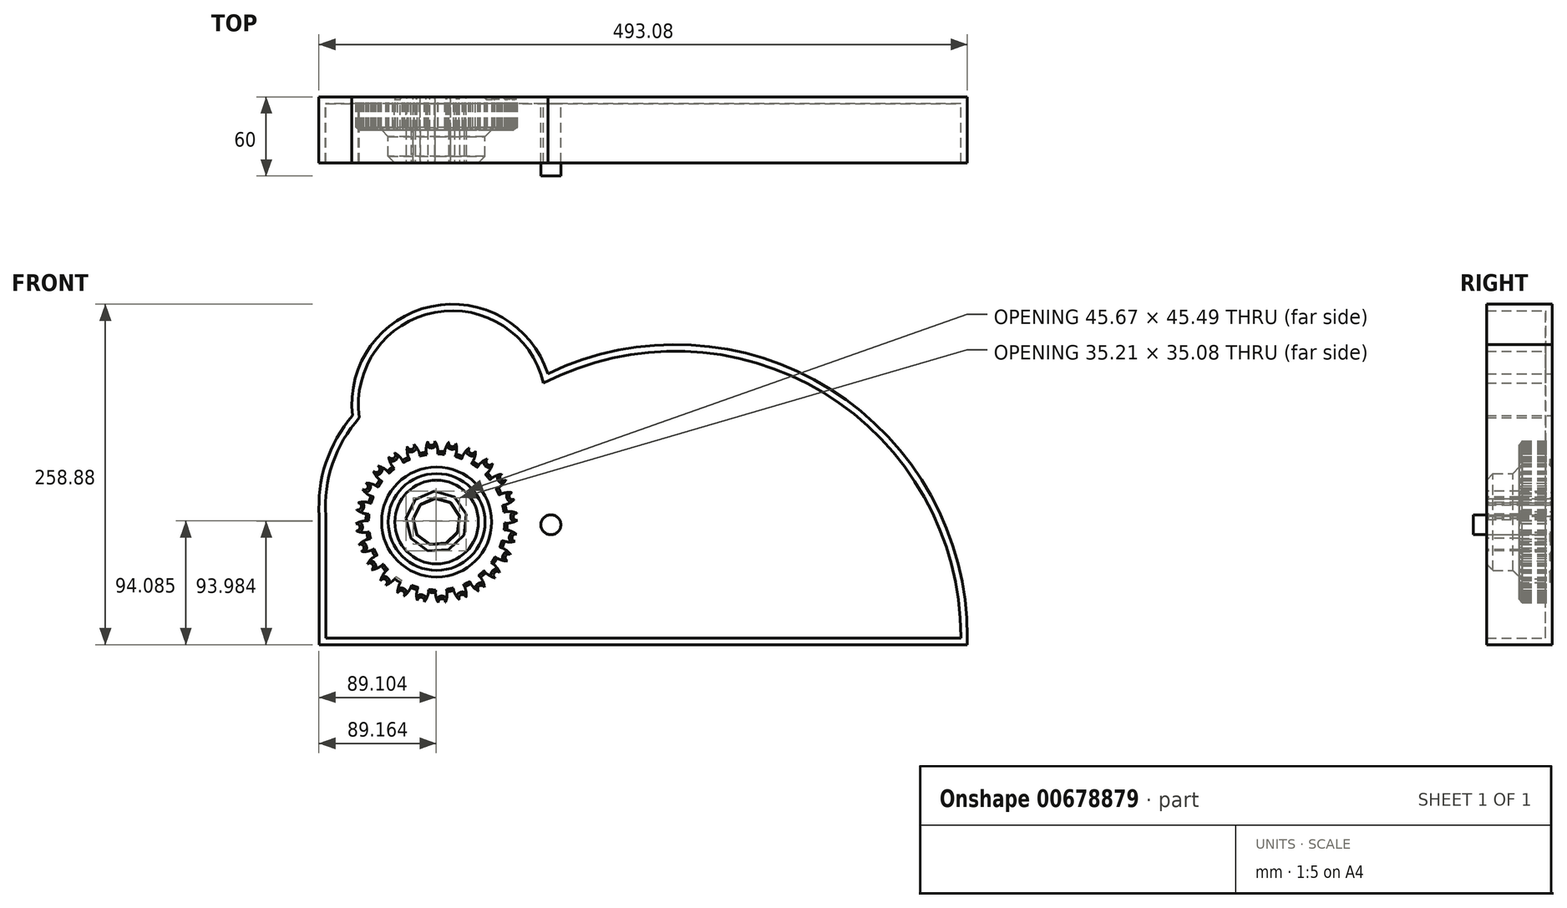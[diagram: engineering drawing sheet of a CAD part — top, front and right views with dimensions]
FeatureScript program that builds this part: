
annotation { "Feature Type Name" : "Feature", "Feature Type Description" : "" }
export const myFeature = defineFeature(function(context is Context, id is Id, definition is map)
    precondition{}
    {
        {
            var Q0;
            Q0=qCreatedBy(makeId("Front.planeOp"),FACE);
            var sketch = newSketch(context, id + "F0", { "sketchPlane" : qUnion([Q0])});
            skCircle(sketch, "E0", {"center": v(0, 0) * mm, "radius": 53.72 * mm});
            skCircle(sketch, "E1", {"center": v(0, 0) * mm, "radius": 58.67 * mm, "construction": true});
            skCircle(sketch, "E2", {"center": v(0, 0) * mm, "radius": 63.5 * mm, "construction": true});
            skLineSegment(sketch, "E3", {"start": v(0, 0) * mm, "end": v(0, 101.64) * mm, "construction": true});
            skLineSegment(sketch, "E4", {"start": v(0, 0) * mm, "end": v(-7.05, 107.5) * mm, "construction": true});
            skLineSegment(sketch, "E5", {"start": v(0, 58.67) * mm, "end": v(-85.15, 58.67) * mm, "construction": true});
            skLineSegment(sketch, "E6", {"start": v(0, 58.67) * mm, "end": v(-80.84, 29.25) * mm, "construction": true});
            skCircle(sketch, "E7", {"center": v(0, 0) * mm, "radius": 55.14 * mm, "construction": true});
            skCircle(sketch, "E8", {"center": v(0, 58.67) * mm, "radius": 14.6 * mm, "construction": true});
            skCircle(sketch, "E9", {"center": v(-13.72, 53.68) * mm, "radius": 14.6 * mm, "construction": true});
            skArc(sketch, "E10", {"start": v(0, 58.67) * mm, "mid": v(-1.19, 61.2) * mm, "end": v(-2.86, 63.44) * mm});
            skArc(sketch, "E11", {"start": v(0.88, 53.71) * mm, "mid": v(0.65, 56.23) * mm, "end": v(0, 58.67) * mm});
            skArc(sketch, "E12.MirrorCS", {"start": v(-7.66, 58.17) * mm, "mid": v(-6.8, 60.83) * mm, "end": v(-5.45, 63.27) * mm});
            skArc(sketch, "E13.MirrorCS", {"start": v(-7.88, 53.14) * mm, "mid": v(-7.98, 55.66) * mm, "end": v(-7.66, 58.17) * mm});
            skArc(sketch, "E14", {"start": v(-5.45, 63.27) * mm, "mid": v(-3.82, 58.31) * mm, "end": v(-2.86, 63.44) * mm});
            skCircle(sketch, "E15", {"center": v(0, 0) * mm, "radius": 36.8 * mm});
            skCircle(sketch, "E16.cCircle", {"center": v(0, 0) * mm, "radius": 17.92 * mm, "construction": true});
            skLineSegment(sketch, "E16.0", {"start": v(7.22, -16.4) * mm, "end": v(-5.01, -17.2) * mm});
            skLineSegment(sketch, "E16.1", {"start": v(-5.01, -17.2) * mm, "end": v(-14.9, -9.95) * mm});
            skLineSegment(sketch, "E16.2", {"start": v(-14.9, -9.95) * mm, "end": v(-17.8, 1.95) * mm});
            skLineSegment(sketch, "E16.3", {"start": v(-17.8, 1.95) * mm, "end": v(-12.39, 12.94) * mm});
            skLineSegment(sketch, "E16.4", {"start": v(-12.39, 12.94) * mm, "end": v(-1.17, 17.88) * mm});
            skLineSegment(sketch, "E16.5", {"start": v(-1.17, 17.88) * mm, "end": v(10.6, 14.45) * mm});
            skLineSegment(sketch, "E16.6", {"start": v(10.6, 14.45) * mm, "end": v(17.4, 4.26) * mm});
            skLineSegment(sketch, "E16.7", {"start": v(17.4, 4.26) * mm, "end": v(16.07, -7.92) * mm});
            skLineSegment(sketch, "E16.8", {"start": v(16.07, -7.92) * mm, "end": v(7.22, -16.4) * mm});
            skSolve(sketch);
        }
        {
            var Q0;
            {var subQ0=sQuery(id+"F0.wireOp",EDGE,"E0");var subQ1=makeQuery(id+"F0.imprint","INTERSECT",VERTEX,{"derivedFrom":[subQ0,sQuery(id+"F0.wireOp",EDGE,"E11")]});Q0=makeQuery(id+"F0.imprint","IMPRINT",FACE,{"disambiguationData":[TD([[makeQuery(id+"F0.imprint","IMPRINT",EDGE,{"disambiguationData":[TD([[subQ1,-1.0]])],"derivedFrom":subQ0}),1.0]])]});}
            var Q1;
            Q1=makeQuery(id+"F0.imprint","IMPRINT",FACE,{"disambiguationData":[TD([[makeQuery(id+"F0.imprint","IMPRINT",EDGE,{"derivedFrom":sQuery(id+"F0.wireOp",EDGE,"E10")}),1.0]])]});
            extrude(context, id + "F1", {"entities" : qUnion([Q0, Q1]), "depth" : 25 * mm, "offsetDistance" : 25 * mm});
        }
        {
            var Q0;
            Q0=makeQuery(id+"F1.opExtrude","SWEPT_BODY",BODY,{"disambiguationData":[OSD([sQuery(id+"F0.wireOp",EDGE,"E0"),sQuery(id+"F0.wireOp",EDGE,"E10"),sQuery(id+"F0.wireOp",EDGE,"E11"),sQuery(id+"F0.wireOp",EDGE,"E12.MirrorCS"),sQuery(id+"F0.wireOp",EDGE,"E13.MirrorCS"),sQuery(id+"F0.wireOp",EDGE,"E14")])]});
            var Q1;
            Q1=makeQuery(id+"F1.opExtrude","SWEPT_FACE",FACE,{"disambiguationData":[OSD([sQuery(id+"F0.wireOp",EDGE,"E0")])]});
            circularPattern(context, id + "F2", {"entities" : qUnion([Q0]), "axis" : qUnion([Q1]), "angle" : 360 * degree, "instanceCount" : 24, "equalSpace" : true});
        }
        {
            var Q0;
            Q0=makeQuery(id+"F0.imprint","IMPRINT",FACE,{"disambiguationData":[TD([[makeQuery(id+"F0.imprint","IMPRINT",EDGE,{"derivedFrom":sQuery(id+"F0.wireOp",EDGE,"E15")}),1.0]])]});
            extrude(context, id + "F3", {"entities" : qUnion([Q0]), "operationType" : NewBodyOperationType.ADD, "depth" : 50 * mm, "offsetDistance" : 25 * mm});
        }
        {
            var Q0;
            Q0=makeQuery(id+"F3.opExtrude","CAP_EDGE",EDGE,{"disambiguationData":[OSD([sQuery(id+"F0.wireOp",EDGE,"E15")])],"isStart":false});
            var Q1;
            Q1=makeQuery(id+"F3.opExtrude","SWEPT_FACE",FACE,{"disambiguationData":[OSD([sQuery(id+"F0.wireOp",EDGE,"E15")])]});
            chamfer(context, id + "F4", {"entities" : qUnion([Q0, Q1]), "width" : 5 * mm, "tangentPropagation" : true});
        }
        {
            var Q0;
            Q0=makeQuery(id+"F2.opPattern","COPY",EDGE,{"derivedFrom":makeQuery(id+"F1.opExtrude","CAP_EDGE",EDGE,{"disambiguationData":[OSD([sQuery(id+"F0.wireOp",EDGE,"E14")])],"isStart":false}),"instanceName":"20"});
            var Q1;
            Q1=makeQuery(id+"F2.opPattern","COPY",EDGE,{"derivedFrom":makeQuery(id+"F1.opExtrude","CAP_EDGE",EDGE,{"disambiguationData":[OSD([sQuery(id+"F0.wireOp",EDGE,"E14")])],"isStart":false}),"instanceName":"10"});
            var Q2;
            Q2=makeQuery(id+"F2.opPattern","COPY",EDGE,{"derivedFrom":makeQuery(id+"F1.opExtrude","CAP_EDGE",EDGE,{"disambiguationData":[OSD([sQuery(id+"F0.wireOp",EDGE,"E14")])],"isStart":true}),"instanceName":"9"});
            var Q3;
            Q3=makeQuery(id+"F2.opPattern","COPY",EDGE,{"derivedFrom":makeQuery(id+"F1.opExtrude","CAP_EDGE",EDGE,{"disambiguationData":[OSD([sQuery(id+"F0.wireOp",EDGE,"E14")])],"isStart":true}),"instanceName":"8"});
            var Q4;
            Q4=makeQuery(id+"F2.opPattern","COPY",EDGE,{"derivedFrom":makeQuery(id+"F1.opExtrude","CAP_EDGE",EDGE,{"disambiguationData":[OSD([sQuery(id+"F0.wireOp",EDGE,"E14")])],"isStart":true}),"instanceName":"7"});
            var Q5;
            Q5=makeQuery(id+"F2.opPattern","COPY",EDGE,{"derivedFrom":makeQuery(id+"F1.opExtrude","CAP_EDGE",EDGE,{"disambiguationData":[OSD([sQuery(id+"F0.wireOp",EDGE,"E14")])],"isStart":false}),"instanceName":"14"});
            var Q6;
            Q6=makeQuery(id+"F2.opPattern","COPY",EDGE,{"derivedFrom":makeQuery(id+"F1.opExtrude","CAP_EDGE",EDGE,{"disambiguationData":[OSD([sQuery(id+"F0.wireOp",EDGE,"E14")])],"isStart":false}),"instanceName":"11"});
            var Q7;
            Q7=makeQuery(id+"F2.opPattern","COPY",EDGE,{"derivedFrom":makeQuery(id+"F1.opExtrude","CAP_EDGE",EDGE,{"disambiguationData":[OSD([sQuery(id+"F0.wireOp",EDGE,"E14")])],"isStart":false}),"instanceName":"9"});
            var Q8;
            Q8=makeQuery(id+"F2.opPattern","COPY",EDGE,{"derivedFrom":makeQuery(id+"F1.opExtrude","CAP_EDGE",EDGE,{"disambiguationData":[OSD([sQuery(id+"F0.wireOp",EDGE,"E14")])],"isStart":false}),"instanceName":"8"});
            var Q9;
            Q9=makeQuery(id+"F2.opPattern","COPY",EDGE,{"derivedFrom":makeQuery(id+"F1.opExtrude","CAP_EDGE",EDGE,{"disambiguationData":[OSD([sQuery(id+"F0.wireOp",EDGE,"E14")])],"isStart":false}),"instanceName":"7"});
            var Q10;
            {var subQ1=sQuery(id+"F0.wireOp",EDGE,"E11");var subQ2=sQuery(id+"F0.wireOp",EDGE,"E0");Q10=makeQuery(id+"F3.boolean.opBoolean","SPLIT",EDGE,{"disambiguationData":[TD([makeQuery(id+"F2.opPattern","COPY",FACE,{"derivedFrom":makeQuery(id+"F1.opExtrude","SWEPT_FACE",FACE,{"disambiguationData":[OSD([subQ1])]}),"instanceName":"13"})])],"derivedFrom":makeQuery(id+"F1.opExtrude","CAP_EDGE",EDGE,{"disambiguationData":[OSD([subQ2])],"isStart":false})});}
            var Q11;
            {var subQ2=sQuery(id+"F0.wireOp",EDGE,"E11");var subQ3=sQuery(id+"F0.wireOp",EDGE,"E0");Q11=makeQuery(id+"F3.boolean.opBoolean","SPLIT",EDGE,{"disambiguationData":[TD([makeQuery(id+"F2.opPattern","COPY",FACE,{"derivedFrom":makeQuery(id+"F1.opExtrude","SWEPT_FACE",FACE,{"disambiguationData":[OSD([subQ2])]}),"instanceName":"14"})])],"derivedFrom":makeQuery(id+"F1.opExtrude","CAP_EDGE",EDGE,{"disambiguationData":[OSD([subQ3])],"isStart":true})});}
            var Q12;
            {var subQ1=sQuery(id+"F0.wireOp",EDGE,"E11");var subQ2=sQuery(id+"F0.wireOp",EDGE,"E0");Q12=makeQuery(id+"F3.boolean.opBoolean","SPLIT",EDGE,{"disambiguationData":[TD([makeQuery(id+"F2.opPattern","COPY",FACE,{"derivedFrom":makeQuery(id+"F1.opExtrude","SWEPT_FACE",FACE,{"disambiguationData":[OSD([subQ1])]}),"instanceName":"15"})])],"derivedFrom":makeQuery(id+"F1.opExtrude","CAP_EDGE",EDGE,{"disambiguationData":[OSD([subQ2])],"isStart":false})});}
            var Q13;
            {var subQ1=sQuery(id+"F0.wireOp",EDGE,"E11");var subQ2=sQuery(id+"F0.wireOp",EDGE,"E0");Q13=makeQuery(id+"F3.boolean.opBoolean","SPLIT",EDGE,{"disambiguationData":[TD([makeQuery(id+"F2.opPattern","COPY",FACE,{"derivedFrom":makeQuery(id+"F1.opExtrude","SWEPT_FACE",FACE,{"disambiguationData":[OSD([subQ1])]}),"instanceName":"18"})])],"derivedFrom":makeQuery(id+"F1.opExtrude","CAP_EDGE",EDGE,{"disambiguationData":[OSD([subQ2])],"isStart":false})});}
            var Q14;
            {var subQ1=sQuery(id+"F0.wireOp",EDGE,"E11");var subQ2=sQuery(id+"F0.wireOp",EDGE,"E0");Q14=makeQuery(id+"F3.boolean.opBoolean","SPLIT",EDGE,{"disambiguationData":[TD([makeQuery(id+"F2.opPattern","COPY",FACE,{"derivedFrom":makeQuery(id+"F1.opExtrude","SWEPT_FACE",FACE,{"disambiguationData":[OSD([subQ1])]}),"instanceName":"19"})])],"derivedFrom":makeQuery(id+"F1.opExtrude","CAP_EDGE",EDGE,{"disambiguationData":[OSD([subQ2])],"isStart":false})});}
            var Q15;
            {var subQ1=sQuery(id+"F0.wireOp",EDGE,"E11");var subQ2=sQuery(id+"F0.wireOp",EDGE,"E0");Q15=makeQuery(id+"F3.boolean.opBoolean","SPLIT",EDGE,{"disambiguationData":[TD([makeQuery(id+"F2.opPattern","COPY",FACE,{"derivedFrom":makeQuery(id+"F1.opExtrude","SWEPT_FACE",FACE,{"disambiguationData":[OSD([subQ1])]}),"instanceName":"20"})])],"derivedFrom":makeQuery(id+"F1.opExtrude","CAP_EDGE",EDGE,{"disambiguationData":[OSD([subQ2])],"isStart":false})});}
            var Q16;
            Q16=makeQuery(id+"F2.opPattern","COPY",EDGE,{"derivedFrom":makeQuery(id+"F1.opExtrude","CAP_EDGE",EDGE,{"disambiguationData":[OSD([sQuery(id+"F0.wireOp",EDGE,"E14")])],"isStart":false}),"instanceName":"22"});
            var Q17;
            Q17=makeQuery(id+"F2.opPattern","COPY",EDGE,{"derivedFrom":makeQuery(id+"F1.opExtrude","CAP_EDGE",EDGE,{"disambiguationData":[OSD([sQuery(id+"F0.wireOp",EDGE,"E14")])],"isStart":false}),"instanceName":"23"});
            var Q18;
            Q18=makeQuery(id+"F1.opExtrude","CAP_EDGE",EDGE,{"disambiguationData":[OSD([sQuery(id+"F0.wireOp",EDGE,"E14")])],"isStart":false});
            var Q19;
            Q19=makeQuery(id+"F2.opPattern","COPY",EDGE,{"derivedFrom":makeQuery(id+"F1.opExtrude","CAP_EDGE",EDGE,{"disambiguationData":[OSD([sQuery(id+"F0.wireOp",EDGE,"E14")])],"isStart":false}),"instanceName":"13"});
            var Q20;
            Q20=makeQuery(id+"F2.opPattern","COPY",EDGE,{"derivedFrom":makeQuery(id+"F1.opExtrude","CAP_EDGE",EDGE,{"disambiguationData":[OSD([sQuery(id+"F0.wireOp",EDGE,"E14")])],"isStart":false}),"instanceName":"12"});
            var Q21;
            {var subQ1=sQuery(id+"F0.wireOp",EDGE,"E11");var subQ2=sQuery(id+"F0.wireOp",EDGE,"E0");Q21=makeQuery(id+"F3.boolean.opBoolean","SPLIT",EDGE,{"disambiguationData":[TD([makeQuery(id+"F2.opPattern","COPY",FACE,{"derivedFrom":makeQuery(id+"F1.opExtrude","SWEPT_FACE",FACE,{"disambiguationData":[OSD([subQ1])]}),"instanceName":"12"})])],"derivedFrom":makeQuery(id+"F1.opExtrude","CAP_EDGE",EDGE,{"disambiguationData":[OSD([subQ2])],"isStart":false})});}
            var Q22;
            {var subQ1=sQuery(id+"F0.wireOp",EDGE,"E11");var subQ2=sQuery(id+"F0.wireOp",EDGE,"E0");Q22=makeQuery(id+"F3.boolean.opBoolean","SPLIT",EDGE,{"disambiguationData":[TD([makeQuery(id+"F2.opPattern","COPY",FACE,{"derivedFrom":makeQuery(id+"F1.opExtrude","SWEPT_FACE",FACE,{"disambiguationData":[OSD([subQ1])]}),"instanceName":"11"})])],"derivedFrom":makeQuery(id+"F1.opExtrude","CAP_EDGE",EDGE,{"disambiguationData":[OSD([subQ2])],"isStart":false})});}
            var Q23;
            {var subQ1=sQuery(id+"F0.wireOp",EDGE,"E11");var subQ2=sQuery(id+"F0.wireOp",EDGE,"E0");Q23=makeQuery(id+"F3.boolean.opBoolean","SPLIT",EDGE,{"disambiguationData":[TD([makeQuery(id+"F2.opPattern","COPY",FACE,{"derivedFrom":makeQuery(id+"F1.opExtrude","SWEPT_FACE",FACE,{"disambiguationData":[OSD([subQ1])]}),"instanceName":"10"})])],"derivedFrom":makeQuery(id+"F1.opExtrude","CAP_EDGE",EDGE,{"disambiguationData":[OSD([subQ2])],"isStart":false})});}
            var Q24;
            {var subQ1=sQuery(id+"F0.wireOp",EDGE,"E11");var subQ2=sQuery(id+"F0.wireOp",EDGE,"E0");Q24=makeQuery(id+"F3.boolean.opBoolean","SPLIT",EDGE,{"disambiguationData":[TD([makeQuery(id+"F2.opPattern","COPY",FACE,{"derivedFrom":makeQuery(id+"F1.opExtrude","SWEPT_FACE",FACE,{"disambiguationData":[OSD([subQ1])]}),"instanceName":"9"})])],"derivedFrom":makeQuery(id+"F1.opExtrude","CAP_EDGE",EDGE,{"disambiguationData":[OSD([subQ2])],"isStart":false})});}
            var Q25;
            {var subQ1=sQuery(id+"F0.wireOp",EDGE,"E11");var subQ2=sQuery(id+"F0.wireOp",EDGE,"E0");Q25=makeQuery(id+"F3.boolean.opBoolean","SPLIT",EDGE,{"disambiguationData":[TD([makeQuery(id+"F2.opPattern","COPY",FACE,{"derivedFrom":makeQuery(id+"F1.opExtrude","SWEPT_FACE",FACE,{"disambiguationData":[OSD([subQ1])]}),"instanceName":"8"})])],"derivedFrom":makeQuery(id+"F1.opExtrude","CAP_EDGE",EDGE,{"disambiguationData":[OSD([subQ2])],"isStart":false})});}
            var Q26;
            {var subQ1=sQuery(id+"F0.wireOp",EDGE,"E11");var subQ2=sQuery(id+"F0.wireOp",EDGE,"E0");Q26=makeQuery(id+"F3.boolean.opBoolean","SPLIT",EDGE,{"disambiguationData":[TD([makeQuery(id+"F2.opPattern","COPY",FACE,{"derivedFrom":makeQuery(id+"F1.opExtrude","SWEPT_FACE",FACE,{"disambiguationData":[OSD([subQ1])]}),"instanceName":"7"})])],"derivedFrom":makeQuery(id+"F1.opExtrude","CAP_EDGE",EDGE,{"disambiguationData":[OSD([subQ2])],"isStart":false})});}
            var Q27;
            {var subQ1=sQuery(id+"F0.wireOp",EDGE,"E11");var subQ2=sQuery(id+"F0.wireOp",EDGE,"E0");Q27=makeQuery(id+"F3.boolean.opBoolean","SPLIT",EDGE,{"disambiguationData":[TD([makeQuery(id+"F2.opPattern","COPY",FACE,{"derivedFrom":makeQuery(id+"F1.opExtrude","SWEPT_FACE",FACE,{"disambiguationData":[OSD([subQ1])]}),"instanceName":"6"})])],"derivedFrom":makeQuery(id+"F1.opExtrude","CAP_EDGE",EDGE,{"disambiguationData":[OSD([subQ2])],"isStart":false})});}
            var Q28;
            Q28=makeQuery(id+"F2.opPattern","COPY",EDGE,{"derivedFrom":makeQuery(id+"F1.opExtrude","CAP_EDGE",EDGE,{"disambiguationData":[OSD([sQuery(id+"F0.wireOp",EDGE,"E14")])],"isStart":false}),"instanceName":"6"});
            var Q29;
            Q29=makeQuery(id+"F2.opPattern","COPY",EDGE,{"derivedFrom":makeQuery(id+"F1.opExtrude","CAP_EDGE",EDGE,{"disambiguationData":[OSD([sQuery(id+"F0.wireOp",EDGE,"E14")])],"isStart":false}),"instanceName":"5"});
            var Q30;
            {var subQ1=sQuery(id+"F0.wireOp",EDGE,"E11");var subQ2=sQuery(id+"F0.wireOp",EDGE,"E0");Q30=makeQuery(id+"F3.boolean.opBoolean","SPLIT",EDGE,{"disambiguationData":[TD([makeQuery(id+"F2.opPattern","COPY",FACE,{"derivedFrom":makeQuery(id+"F1.opExtrude","SWEPT_FACE",FACE,{"disambiguationData":[OSD([subQ1])]}),"instanceName":"4"})])],"derivedFrom":makeQuery(id+"F1.opExtrude","CAP_EDGE",EDGE,{"disambiguationData":[OSD([subQ2])],"isStart":false})});}
            var Q31;
            {var subQ1=sQuery(id+"F0.wireOp",EDGE,"E11");var subQ2=sQuery(id+"F0.wireOp",EDGE,"E0");Q31=makeQuery(id+"F3.boolean.opBoolean","SPLIT",EDGE,{"disambiguationData":[TD([makeQuery(id+"F2.opPattern","COPY",FACE,{"derivedFrom":makeQuery(id+"F1.opExtrude","SWEPT_FACE",FACE,{"disambiguationData":[OSD([subQ1])]}),"instanceName":"5"})])],"derivedFrom":makeQuery(id+"F1.opExtrude","CAP_EDGE",EDGE,{"disambiguationData":[OSD([subQ2])],"isStart":false})});}
            var Q32;
            Q32=makeQuery(id+"F2.opPattern","COPY",EDGE,{"derivedFrom":makeQuery(id+"F1.opExtrude","CAP_EDGE",EDGE,{"disambiguationData":[OSD([sQuery(id+"F0.wireOp",EDGE,"E14")])],"isStart":false}),"instanceName":"21"});
            var Q33;
            {var subQ1=sQuery(id+"F0.wireOp",EDGE,"E11");var subQ2=sQuery(id+"F0.wireOp",EDGE,"E0");Q33=makeQuery(id+"F3.boolean.opBoolean","SPLIT",EDGE,{"disambiguationData":[TD([makeQuery(id+"F2.opPattern","COPY",FACE,{"derivedFrom":makeQuery(id+"F1.opExtrude","SWEPT_FACE",FACE,{"disambiguationData":[OSD([subQ1])]}),"instanceName":"21"})])],"derivedFrom":makeQuery(id+"F1.opExtrude","CAP_EDGE",EDGE,{"disambiguationData":[OSD([subQ2])],"isStart":false})});}
            var Q34;
            {var subQ1=sQuery(id+"F0.wireOp",EDGE,"E11");var subQ2=sQuery(id+"F0.wireOp",EDGE,"E0");Q34=makeQuery(id+"F3.boolean.opBoolean","SPLIT",EDGE,{"disambiguationData":[TD([makeQuery(id+"F2.opPattern","COPY",FACE,{"derivedFrom":makeQuery(id+"F1.opExtrude","SWEPT_FACE",FACE,{"disambiguationData":[OSD([subQ1])]}),"instanceName":"22"})])],"derivedFrom":makeQuery(id+"F1.opExtrude","CAP_EDGE",EDGE,{"disambiguationData":[OSD([subQ2])],"isStart":false})});}
            var Q35;
            Q35=makeQuery(id+"F2.opPattern","COPY",EDGE,{"derivedFrom":makeQuery(id+"F1.opExtrude","CAP_EDGE",EDGE,{"disambiguationData":[OSD([sQuery(id+"F0.wireOp",EDGE,"E14")])],"isStart":false}),"instanceName":"18"});
            var Q36;
            Q36=makeQuery(id+"F2.opPattern","COPY",EDGE,{"derivedFrom":makeQuery(id+"F1.opExtrude","CAP_EDGE",EDGE,{"disambiguationData":[OSD([sQuery(id+"F0.wireOp",EDGE,"E14")])],"isStart":false}),"instanceName":"17"});
            var Q37;
            Q37=makeQuery(id+"F2.opPattern","COPY",EDGE,{"derivedFrom":makeQuery(id+"F1.opExtrude","CAP_EDGE",EDGE,{"disambiguationData":[OSD([sQuery(id+"F0.wireOp",EDGE,"E14")])],"isStart":false}),"instanceName":"16"});
            var Q38;
            {var subQ1=sQuery(id+"F0.wireOp",EDGE,"E11");var subQ2=sQuery(id+"F0.wireOp",EDGE,"E0");Q38=makeQuery(id+"F3.boolean.opBoolean","SPLIT",EDGE,{"disambiguationData":[TD([makeQuery(id+"F2.opPattern","COPY",FACE,{"derivedFrom":makeQuery(id+"F1.opExtrude","SWEPT_FACE",FACE,{"disambiguationData":[OSD([subQ1])]}),"instanceName":"16"})])],"derivedFrom":makeQuery(id+"F1.opExtrude","CAP_EDGE",EDGE,{"disambiguationData":[OSD([subQ2])],"isStart":false})});}
            var Q39;
            {var subQ1=sQuery(id+"F0.wireOp",EDGE,"E11");var subQ2=sQuery(id+"F0.wireOp",EDGE,"E0");Q39=makeQuery(id+"F3.boolean.opBoolean","SPLIT",EDGE,{"disambiguationData":[TD([makeQuery(id+"F2.opPattern","COPY",FACE,{"derivedFrom":makeQuery(id+"F1.opExtrude","SWEPT_FACE",FACE,{"disambiguationData":[OSD([subQ1])]}),"instanceName":"17"})])],"derivedFrom":makeQuery(id+"F1.opExtrude","CAP_EDGE",EDGE,{"disambiguationData":[OSD([subQ2])],"isStart":false})});}
            var Q40;
            {var subQ0=sQuery(id+"F0.wireOp",EDGE,"E13.MirrorCS");var subQ2=sQuery(id+"F0.wireOp",EDGE,"E0");Q40=makeQuery(id+"F3.boolean.opBoolean","SPLIT",EDGE,{"disambiguationData":[TD([makeQuery(id+"F1.opExtrude","SWEPT_FACE",FACE,{"disambiguationData":[OSD([subQ0])]})])],"derivedFrom":makeQuery(id+"F1.opExtrude","CAP_EDGE",EDGE,{"disambiguationData":[OSD([subQ2])],"isStart":false})});}
            var Q41;
            {var subQ1=sQuery(id+"F0.wireOp",EDGE,"E11");var subQ2=sQuery(id+"F0.wireOp",EDGE,"E0");Q41=makeQuery(id+"F3.boolean.opBoolean","SPLIT",EDGE,{"disambiguationData":[TD([makeQuery(id+"F1.opExtrude","SWEPT_FACE",FACE,{"disambiguationData":[OSD([subQ1])]})])],"derivedFrom":makeQuery(id+"F1.opExtrude","CAP_EDGE",EDGE,{"disambiguationData":[OSD([subQ2])],"isStart":false})});}
            var Q42;
            {var subQ1=sQuery(id+"F0.wireOp",EDGE,"E11");var subQ2=sQuery(id+"F0.wireOp",EDGE,"E0");Q42=makeQuery(id+"F3.boolean.opBoolean","SPLIT",EDGE,{"disambiguationData":[TD([makeQuery(id+"F2.opPattern","COPY",FACE,{"derivedFrom":makeQuery(id+"F1.opExtrude","SWEPT_FACE",FACE,{"disambiguationData":[OSD([subQ1])]}),"instanceName":"1"})])],"derivedFrom":makeQuery(id+"F1.opExtrude","CAP_EDGE",EDGE,{"disambiguationData":[OSD([subQ2])],"isStart":false})});}
            var Q43;
            {var subQ1=sQuery(id+"F0.wireOp",EDGE,"E11");var subQ2=sQuery(id+"F0.wireOp",EDGE,"E0");Q43=makeQuery(id+"F3.boolean.opBoolean","SPLIT",EDGE,{"disambiguationData":[TD([makeQuery(id+"F2.opPattern","COPY",FACE,{"derivedFrom":makeQuery(id+"F1.opExtrude","SWEPT_FACE",FACE,{"disambiguationData":[OSD([subQ1])]}),"instanceName":"2"})])],"derivedFrom":makeQuery(id+"F1.opExtrude","CAP_EDGE",EDGE,{"disambiguationData":[OSD([subQ2])],"isStart":false})});}
            var Q44;
            Q44=makeQuery(id+"F2.opPattern","COPY",EDGE,{"derivedFrom":makeQuery(id+"F1.opExtrude","CAP_EDGE",EDGE,{"disambiguationData":[OSD([sQuery(id+"F0.wireOp",EDGE,"E14")])],"isStart":false}),"instanceName":"1"});
            var Q45;
            Q45=makeQuery(id+"F2.opPattern","COPY",EDGE,{"derivedFrom":makeQuery(id+"F1.opExtrude","CAP_EDGE",EDGE,{"disambiguationData":[OSD([sQuery(id+"F0.wireOp",EDGE,"E14")])],"isStart":false}),"instanceName":"2"});
            var Q46;
            Q46=makeQuery(id+"F2.opPattern","COPY",EDGE,{"derivedFrom":makeQuery(id+"F1.opExtrude","CAP_EDGE",EDGE,{"disambiguationData":[OSD([sQuery(id+"F0.wireOp",EDGE,"E14")])],"isStart":true}),"instanceName":"3"});
            var Q47;
            Q47=makeQuery(id+"F2.opPattern","COPY",EDGE,{"derivedFrom":makeQuery(id+"F1.opExtrude","CAP_EDGE",EDGE,{"disambiguationData":[OSD([sQuery(id+"F0.wireOp",EDGE,"E14")])],"isStart":false}),"instanceName":"15"});
            var Q48;
            {var subQ1=sQuery(id+"F0.wireOp",EDGE,"E11");var subQ2=sQuery(id+"F0.wireOp",EDGE,"E0");Q48=makeQuery(id+"F3.boolean.opBoolean","SPLIT",EDGE,{"disambiguationData":[TD([makeQuery(id+"F2.opPattern","COPY",FACE,{"derivedFrom":makeQuery(id+"F1.opExtrude","SWEPT_FACE",FACE,{"disambiguationData":[OSD([subQ1])]}),"instanceName":"3"})])],"derivedFrom":makeQuery(id+"F1.opExtrude","CAP_EDGE",EDGE,{"disambiguationData":[OSD([subQ2])],"isStart":false})});}
            var Q49;
            Q49=makeQuery(id+"F2.opPattern","COPY",EDGE,{"derivedFrom":makeQuery(id+"F1.opExtrude","CAP_EDGE",EDGE,{"disambiguationData":[OSD([sQuery(id+"F0.wireOp",EDGE,"E14")])],"isStart":false}),"instanceName":"4"});
            var Q50;
            Q50=makeQuery(id+"F2.opPattern","COPY",EDGE,{"derivedFrom":makeQuery(id+"F1.opExtrude","CAP_EDGE",EDGE,{"disambiguationData":[OSD([sQuery(id+"F0.wireOp",EDGE,"E14")])],"isStart":false}),"instanceName":"19"});
            var Q51;
            Q51=makeQuery(id+"F2.opPattern","COPY",EDGE,{"derivedFrom":makeQuery(id+"F1.opExtrude","CAP_EDGE",EDGE,{"disambiguationData":[OSD([sQuery(id+"F0.wireOp",EDGE,"E14")])],"isStart":false}),"instanceName":"3"});
            chamfer(context, id + "F5", {"entities" : qUnion([Q0, Q1, Q2, Q3, Q4, Q5, Q6, Q7, Q8, Q9, Q10, Q11, Q12, Q13, Q14, Q15, Q16, Q17, Q18, Q19, Q20, Q21, Q22, Q23, Q24, Q25, Q26, Q27, Q28, Q29, Q30, Q31, Q32, Q33, Q34, Q35, Q36, Q37, Q38, Q39, Q40, Q41, Q42, Q43, Q44, Q45, Q46, Q47, Q48, Q49, Q50, Q51]), "width" : 2 * mm, "tangentPropagation" : true});
        }
        {
            var Q0;
            Q0=qCreatedBy(makeId("Front.planeOp"),FACE);
            var sketch = newSketch(context, id + "F6", { "sketchPlane" : qUnion([Q0])});
            skLineSegment(sketch, "E17", {"start": v(-89.2, -93.22) * mm, "end": v(403.6, -93.22) * mm});
            skLineSegment(sketch, "E18", {"start": v(403.6, -93.22) * mm, "end": v(403.6, -87.36) * mm});
            skLineSegment(sketch, "E19", {"start": v(-89.2, -93.22) * mm, "end": v(-89.2, 4.46) * mm});
            skArc(sketch, "E20", {"start": v(-64, 80.81) * mm, "mid": v(-84.17, 45.14) * mm, "end": v(-89.2, 4.46) * mm});
            skArc(sketch, "E21", {"start": v(84.54, 112.77) * mm, "mid": v(-4.18, 163.96) * mm, "end": v(-64, 80.81) * mm});
            skArc(sketch, "E22", {"start": v(403.6, -87.36) * mm, "mid": v(299.43, 100.95) * mm, "end": v(84.54, 112.77) * mm});
            skLineSegment(sketch, "E23.0", {"start": v(7.1, -15.97) * mm, "end": v(-5.13, -16.77) * mm});
            skLineSegment(sketch, "E23.1", {"start": v(-5.13, -16.77) * mm, "end": v(-15, -9.53) * mm});
            skLineSegment(sketch, "E23.2", {"start": v(-15, -9.53) * mm, "end": v(-17.92, 2.38) * mm});
            skLineSegment(sketch, "E23.3", {"start": v(-17.92, 2.38) * mm, "end": v(-12.5, 13.37) * mm});
            skLineSegment(sketch, "E23.4", {"start": v(-12.5, 13.37) * mm, "end": v(-1.28, 18.3) * mm});
            skLineSegment(sketch, "E23.5", {"start": v(-1.28, 18.3) * mm, "end": v(10.48, 14.87) * mm});
            skLineSegment(sketch, "E23.6", {"start": v(10.48, 14.87) * mm, "end": v(17.29, 4.68) * mm});
            skLineSegment(sketch, "E23.7", {"start": v(17.29, 4.68) * mm, "end": v(15.96, -7.5) * mm});
            skLineSegment(sketch, "E23.8", {"start": v(15.96, -7.5) * mm, "end": v(7.1, -15.97) * mm});
            skCircle(sketch, "E24", {"center": v(137.55, 0) * mm, "radius": 16.16 * mm});
            skSolve(sketch);
        }
        {
            var Q0;
            Q0=makeQuery(id+"F6.imprint","IMPRINT",FACE,{"disambiguationData":[TD([[makeQuery(id+"F6.imprint","IMPRINT",EDGE,{"derivedFrom":sQuery(id+"F6.wireOp",EDGE,"E17")}),1.0]])]});
            var Q1;
            Q1=makeQuery(id+"F6.imprint","IMPRINT",FACE,{"disambiguationData":[TD([[makeQuery(id+"F6.imprint","IMPRINT",EDGE,{"derivedFrom":sQuery(id+"F6.wireOp",EDGE,"E24")}),1.0]])]});
            extrude(context, id + "F7", {"entities" : qUnion([Q0, Q1]), "depth" : 50 * mm, "offsetDistance" : 25 * mm});
        }
        {
            var Q0;
            Q0=makeQuery(id+"F7.opExtrude","CAP_FACE",FACE,{"disambiguationData":[OSD([sQuery(id+"F6.wireOp",EDGE,"E17"),sQuery(id+"F6.wireOp",EDGE,"E18"),sQuery(id+"F6.wireOp",EDGE,"E19"),sQuery(id+"F6.wireOp",EDGE,"E20"),sQuery(id+"F6.wireOp",EDGE,"E21"),sQuery(id+"F6.wireOp",EDGE,"E22")])],"isStart":false});
            shell(context, id + "F8", {"entities" : qUnion([Q0]), "thickness" : 5 * mm});
        }
        {
            var Q0;
            Q0=makeQuery(id+"F7.opExtrude","CAP_FACE",FACE,{"disambiguationData":[OSD([sQuery(id+"F6.wireOp",EDGE,"E17"),sQuery(id+"F6.wireOp",EDGE,"E18"),sQuery(id+"F6.wireOp",EDGE,"E19"),sQuery(id+"F6.wireOp",EDGE,"E20"),sQuery(id+"F6.wireOp",EDGE,"E21"),sQuery(id+"F6.wireOp",EDGE,"E22"),sQuery(id+"F6.wireOp",EDGE,"E23.0"),sQuery(id+"F6.wireOp",EDGE,"E23.1"),sQuery(id+"F6.wireOp",EDGE,"E23.2"),sQuery(id+"F6.wireOp",EDGE,"E23.3"),sQuery(id+"F6.wireOp",EDGE,"E23.4"),sQuery(id+"F6.wireOp",EDGE,"E23.5"),sQuery(id+"F6.wireOp",EDGE,"E23.6"),sQuery(id+"F6.wireOp",EDGE,"E23.7"),sQuery(id+"F6.wireOp",EDGE,"E23.8")])],"isStart":false});
            extrude(context, id + "F9", {"entities" : qUnion([Q0]), "operationType" : NewBodyOperationType.REMOVE, "oppositeDirection" : true, "depth" : 25 * mm, "offsetDistance" : 25 * mm});
        }
        {
            var Q0;
            {var subQ0=sQuery(id+"F6.wireOp",EDGE,"E23.8");var subQ1=sQuery(id+"F6.wireOp",EDGE,"E23.7");var subQ2=sQuery(id+"F6.wireOp",EDGE,"E23.6");var subQ3=sQuery(id+"F6.wireOp",EDGE,"E23.5");var subQ4=sQuery(id+"F6.wireOp",EDGE,"E23.4");var subQ5=sQuery(id+"F6.wireOp",EDGE,"E23.3");var subQ6=sQuery(id+"F6.wireOp",EDGE,"E23.2");var subQ7=sQuery(id+"F6.wireOp",EDGE,"E23.1");var subQ8=sQuery(id+"F6.wireOp",EDGE,"E23.0");var subQ9=sQuery(id+"F6.wireOp",EDGE,"E22");var subQ10=sQuery(id+"F6.wireOp",EDGE,"E21");var subQ11=sQuery(id+"F6.wireOp",EDGE,"E20");var subQ12=sQuery(id+"F6.wireOp",EDGE,"E19");var subQ13=sQuery(id+"F6.wireOp",EDGE,"E18");var subQ14=sQuery(id+"F6.wireOp",EDGE,"E17");Q0=makeQuery(id+"F8.opShell","OFFSET_FACE",FACE,{"disambiguationData":[OSD([subQ14,subQ13,subQ12,subQ11,subQ10,subQ9,subQ8,subQ7,subQ6,subQ5,subQ4,subQ3,subQ2,subQ1,subQ0]),TDD([makeQuery(id+"F7.opExtrude","CAP_FACE",FACE,{"disambiguationData":[OSD([subQ14,subQ13,subQ12,subQ11,subQ10,subQ9,subQ8,subQ7,subQ6,subQ5,subQ4,subQ3,subQ2,subQ1,subQ0])],"isStart":true})])]});}
            var sketch = newSketch(context, id + "F10", { "sketchPlane" : qUnion([Q0])});
            skCircle(sketch, "E25", {"center": v(86.9, -2.1) * mm, "radius": 7.59 * mm});
            skSolve(sketch);
        }
        {
            var Q0;
            Q0 = qSketchRegion(id + "F10", true);
            extrude(context, id + "F11", {"entities" : qUnion([Q0]), "operationType" : NewBodyOperationType.ADD, "depth" : 55 * mm, "offsetDistance" : 25 * mm});
        }
    });
